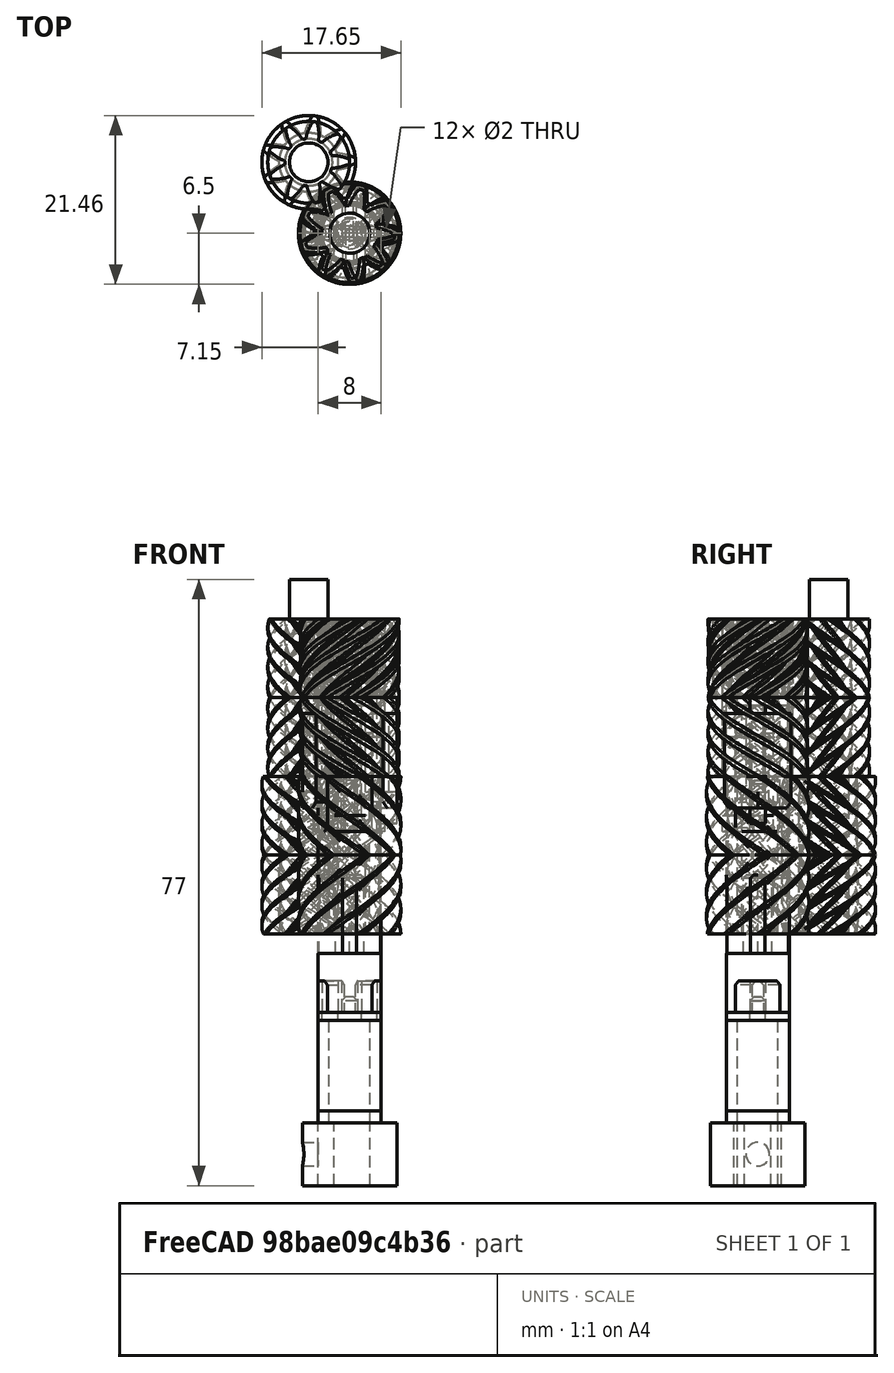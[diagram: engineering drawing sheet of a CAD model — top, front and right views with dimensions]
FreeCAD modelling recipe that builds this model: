
FCSTD DOCUMENT  (FreeCAD 0.19R24276 (Git))
Label: G-mini_inner-gear_011
License: All rights reserved
LicenseURL: http://en.wikipedia.org/wiki/All_rights_reserved
objects: Part::Cylinder×51, Part::Cut×37, Part::Compound×25, Part::FeaturePython×15, Part::Box×13, Part::Chamfer×11, Mesh::Feature×4
note: 152 computed .brp shape members not serialized (recipe doc carries the construction recipe); baked Part::Feature solids carry a one-line shape summary decoded from their .brp

FEATURE [Part::Cylinder] Cylinder016  label="Válec016"
  Angle = 360
  AttacherType = Attacher::AttachEngine3D
  Height = 60
  Placement = pos=(10.4,0,-20) rot=(0,0,1;0rad)
  Radius = 2.55
FEATURE [Part::Cylinder] Cylinder017  label="Válec017"
  Angle = 360
  AttacherType = Attacher::AttachEngine3D
  Height = 60
  Placement = pos=(10.4,0,40) rot=(0,0,1;0rad)
  Radius = 2.55
FEATURE [Part::Cylinder] Cylinder018  label="Válec018"
  Angle = 360
  AttacherType = Attacher::AttachEngine3D
  Height = 60
  Placement = pos=(10.4,0,-20) rot=(0,0,1;0rad)
  Radius = 2.55
FEATURE [Part::Cylinder] Cylinder019  label="Válec019"
  Angle = 360
  AttacherType = Attacher::AttachEngine3D
  Height = 60
  Placement = pos=(10.4,0,40) rot=(0,0,1;0rad)
  Radius = 2.55
FEATURE [Part::FeaturePython] wormgear025  # WARN: FeaturePython — macro-defined, semantics opaque (R4)
  AttacherType = Attacher::AttachEngine3D
  Placement = pos=(10.4,0,0) rot=(0,0,1;0.977384rad)
  beta = 37.1583
  clearance = 0.25
  diameter = 9.5
  head = 0.5
  height = 10
  module = 0.8
  pressure_angle = 20
  reverse_pitch = true
  teeth = 9
  version = 0.0.3
FEATURE [Part::Cut] Cut005
  Base = -> wormgear025
  Tool = -> Cylinder018
FEATURE [Part::FeaturePython] wormgear031  # WARN: FeaturePython — macro-defined, semantics opaque (R4)
  AttacherType = Attacher::AttachEngine3D
  Placement = pos=(10.4,0,-10) rot=(0,0,1;0.991347rad)
  beta = 37.1583
  clearance = 0.25
  diameter = 9.5
  head = 0.5
  height = 10
  module = 0.8
  pressure_angle = 20
  reverse_pitch = false
  teeth = 9
  version = 0.0.3
FEATURE [Part::Cut] Cut002
  Base = -> wormgear031
  Tool = -> Cylinder016
FEATURE [Part::FeaturePython] wormgear032  # WARN: FeaturePython — macro-defined, semantics opaque (R4)
  AttacherType = Attacher::AttachEngine3D
  Placement = pos=(10.4,0,20) rot=(0,0,1;0.959931rad)
  beta = 41.9872
  clearance = 0.25
  diameter = 8
  head = 0.5
  height = 10
  module = 0.8
  pressure_angle = 20
  reverse_pitch = true
  teeth = 9
  version = 0.0.3
FEATURE [Part::Cut] Cut003
  Base = -> wormgear032
  Tool = -> Cylinder019
FEATURE [Part::FeaturePython] wormgear033  # WARN: FeaturePython — macro-defined, semantics opaque (R4)
  AttacherType = Attacher::AttachEngine3D
  Placement = pos=(10.4,0,10) rot=(0,0,1;0.977384rad)
  beta = 41.9872
  clearance = 0.25
  diameter = 8
  head = 0.5
  height = 10
  module = 0.8
  pressure_angle = 20
  reverse_pitch = false
  teeth = 9
  version = 0.0.3
FEATURE [Part::Cut] Cut004
  Base = -> wormgear033
  Tool = -> Cylinder017
FEATURE [Part::Compound] Compound002  label="gearovina-mini_vnejsi-kolecko_1"
  Links = -> [Cut002,Cut004,Cut003,Cut005]
FEATURE [Part::Cylinder] Cylinder025  label="Válec025"
  Angle = 360
  AttacherType = Attacher::AttachEngine3D
  Height = 5
  Placement = pos=(10.4,0,30) rot=(0,0,1;0rad)
  Radius = 2.45
FEATURE [Part::Compound] Compound007  label="gearovina-mini_vnejsi-kolecko001"
  Links = -> [Compound002,Cylinder025]
  Placement = pos=(0,0,0) rot=(0,0,1;2.0944rad)
FEATURE [Part::Cylinder] Cylinder028  label="Válec028"
  Angle = 360
  AttacherType = Attacher::AttachEngine3D
  Height = 60
  Placement = pos=(0,0,-20) rot=(0,0,1;0rad)
  Radius = 2.55
FEATURE [Part::Cylinder] Cylinder029  label="Válec029"
  Angle = 360
  AttacherType = Attacher::AttachEngine3D
  Height = 60
  Placement = pos=(0,0,-20) rot=(0,0,1;0rad)
  Radius = 2.55
FEATURE [Part::FeaturePython] wormgear036  # WARN: FeaturePython — macro-defined, semantics opaque (R4)
  AttacherType = Attacher::AttachEngine3D
  Placement = pos=(0,0,0) rot=(0,0,1;1.11876rad)
  beta = 41.9872
  clearance = 0.1
  diameter = 10
  head = 0.5
  height = 10
  module = 1
  pressure_angle = 20
  reverse_pitch = true
  teeth = 9
  version = 0.0.3
FEATURE [Part::Cut] Cut009
  Base = -> wormgear036
  Tool = -> Cylinder028
FEATURE [Part::FeaturePython] wormgear037  # WARN: FeaturePython — macro-defined, semantics opaque (R4)
  AttacherType = Attacher::AttachEngine3D
  Placement = pos=(0,0,-10) rot=(0,0,1;0.991347rad)
  beta = 41.9872
  clearance = 0.1
  diameter = 10
  head = 0.5
  height = 10
  module = 1
  pressure_angle = 20
  reverse_pitch = false
  teeth = 9
  version = 0.0.3
FEATURE [Part::Cut] Cut008
  Base = -> wormgear037
  Tool = -> Cylinder029
FEATURE [Part::Compound] Compound1283  label="G-midi_outer-gear"
  Links = -> [Cut009,Cut008]
FEATURE [Part::FeaturePython] Tube001  # WARN: FeaturePython — macro-defined, semantics opaque (R4)
  AttacherType = Attacher::AttachEngine3D
  Height = 10
  InnerRadius = 2
  OuterRadius = 4
  Placement = pos=(0,0,-10) rot=(0,0,1;0rad)
FEATURE [Part::Cylinder] Cylinder  label="Válec"
  Angle = 360
  AttacherType = Attacher::AttachEngine3D
  Height = 10
  Radius = 4
FEATURE [Part::FeaturePython] wormgear035  # WARN: FeaturePython — macro-defined, semantics opaque (R4)
  AttacherType = Attacher::AttachEngine3D
  Placement = pos=(0,0,20) rot=(0,0,1;1.6057rad)
  beta = 33.2066
  clearance = 0.25
  diameter = 11
  head = 0
  height = 10
  module = 0.8
  pressure_angle = 20
  reverse_pitch = false
  teeth = 9
  version = 0.0.3
FEATURE [Part::FeaturePython] wormgear038  # WARN: FeaturePython — macro-defined, semantics opaque (R4)
  AttacherType = Attacher::AttachEngine3D
  Placement = pos=(0,0,10) rot=(0,0,1;1.6057rad)
  beta = 33.2066
  clearance = 0.25
  diameter = 11
  head = 0
  height = 10
  module = 0.8
  pressure_angle = 20
  reverse_pitch = true
  teeth = 9
  version = 0.0.3
FEATURE [Part::Compound] Compound011
  Links = -> [wormgear035,wormgear038,Tube001,Cylinder]
FEATURE [Part::Cylinder] Cylinder2021  label="Válec2021"
  Angle = 360
  AttacherType = Attacher::AttachEngine3D
  Height = 12
  Placement = pos=(0,0,-20) rot=(0,0,1;0rad)
  Radius = 4
FEATURE [Part::Cylinder] Cylinder2022  label="Válec2022"
  Angle = 360
  AttacherType = Attacher::AttachEngine3D
  Height = 6
  Placement = pos=(0,0,-14) rot=(0,0,1;0rad)
  Radius = 2
FEATURE [Part::Cylinder] Cylinder2023  label="Válec2023"
  Angle = 360
  AttacherType = Attacher::AttachEngine3D
  Height = 20
  Placement = pos=(-4,0,-20) rot=(0,0,-1;1.5708rad)
  Radius = 1
FEATURE [Part::Cylinder] Cylinder2024  label="Válec2024"
  Angle = 360
  AttacherType = Attacher::AttachEngine3D
  Height = 12
  Placement = pos=(0,0,-20) rot=(0,0,1;0rad)
  Radius = 1
FEATURE [Part::FeaturePython] wormgear073  # WARN: FeaturePython — macro-defined, semantics opaque (R4)
  AttacherType = Attacher::AttachEngine3D
  Placement = pos=(0,0,20) rot=(0,0,1;0.881391rad)
  beta = 38.6598
  clearance = 0.25
  diameter = 9
  head = 0.5
  height = 10
  module = 0.8
  pressure_angle = 20
  reverse_pitch = false
  teeth = 9
  version = 0.0.3
FEATURE [Part::Cut] Cut481
  Base = -> Cylinder2021
  Tool = -> Cylinder2024
FEATURE [Part::Box] Box421  label="Krychle421"
  AttacherType = Attacher::AttachEngine3D
  Height = 12
  Length = 16
  Placement = pos=(5.65685,-5.65685,-20) rot=(0,0,1;2.35619rad)
  Width = 8
FEATURE [Part::Cut] Cut485
  Base = -> Cut481
  Tool = -> Box421
FEATURE [Part::Cylinder] Cylinder2025  label="Válec2025"
  Angle = 360
  AttacherType = Attacher::AttachEngine3D
  Height = 20
  Placement = pos=(4,0,-20) rot=(0,0,-1;1.5708rad)
  Radius = 1
FEATURE [Part::Compound] Compound650
  Links = -> [Cylinder2025,Cylinder2023]
  Placement = pos=(0,0,24) rot=(0,0,1;0rad)
FEATURE [Part::Cylinder] Cylinder2026  label="Válec2026"
  Angle = 360
  AttacherType = Attacher::AttachEngine3D
  Height = 2
  Placement = pos=(-4,0,-20) rot=(0,0,-1;1.5708rad)
  Radius = 2
FEATURE [Part::Cylinder] Cylinder2027  label="Válec2027"
  Angle = 360
  AttacherType = Attacher::AttachEngine3D
  Height = 2
  Placement = pos=(0,0,18) rot=(0,0,1;0rad)
  Radius = 4
FEATURE [Part::Compound] Compound647
  Links = -> [wormgear073,Cylinder2027]
FEATURE [Part::Cylinder] Cylinder2028  label="Válec2028"
  Angle = 360
  AttacherType = Attacher::AttachEngine3D
  Height = 15
  Placement = pos=(0,0,19) rot=(0,0,1;0rad)
  Radius = 2.6
FEATURE [Part::Cut] Cut480
  Base = -> Compound647
  Tool = -> Cylinder2028
FEATURE [Part::Cut] Cut483
  Base = -> Cut480
  Tool = -> Compound650
FEATURE [Part::Cylinder] Cylinder2029  label="Válec2029"
  Angle = 360
  AttacherType = Attacher::AttachEngine3D
  Height = 20
  Placement = pos=(4,0,-20) rot=(0,0,-1;1.5708rad)
  Radius = 1
FEATURE [Part::Cylinder] Cylinder2030  label="Válec2030"
  Angle = 360
  AttacherType = Attacher::AttachEngine3D
  Height = 2
  Placement = pos=(4,0,-20) rot=(0,0,-1;1.5708rad)
  Radius = 2
FEATURE [Part::Compound] Compound651
  Links = -> [Cylinder2030,Cylinder2026]
  Placement = pos=(0,0,24) rot=(0,0,1;0rad)
FEATURE [Part::Box] Box422  label="Krychle422"
  AttacherType = Attacher::AttachEngine3D
  Height = 12
  Length = 16
  Placement = pos=(-5.65685,-5.65685,-20) rot=(0,0,1;0.785398rad)
  Width = 8
FEATURE [Part::Cut] Cut487
  Base = -> Cut485
  Tool = -> Box422
FEATURE [Part::Cut] Cut484
  Base = -> Cut487
  Placement = pos=(0,0,0) rot=(0,0,1;3.14159rad)
  Tool = -> Cylinder2029
FEATURE [Part::Cut] Cut486
  Base = -> Cut487
  Tool = -> Cylinder2029
FEATURE [Part::Compound] Compound649  label="G-midi_sun-sym-mixo004"
  Links = -> [Cut486,Cut484,Cylinder2022]
  Placement = pos=(0,0,26) rot=(0,0,1;0rad)
FEATURE [Part::Chamfer] Chamfer018
  Base = -> Compound649
  Edges = 4 edges r=0.75: [Edge8,Edge11,Edge29,Edge32]
FEATURE [Part::Cut] Cut482
  Base = -> Chamfer018
  Tool = -> Compound651
FEATURE [Part::Chamfer] Chamfer019
  Base = -> Cut482
  Edges = 1 edges r=0.5: [Edge75]
FEATURE [Part::Compound] Compound648  label="G-midi_inner-gear-part-A-lax"
  Links = -> [Cut483,Chamfer019]
FEATURE [Part::Cylinder] Cylinder2031  label="Válec2031"
  Angle = 360
  AttacherType = Attacher::AttachEngine3D
  Height = 12
  Placement = pos=(0,0,-20) rot=(0,0,1;0rad)
  Radius = 4
FEATURE [Part::Cylinder] Cylinder2032  label="Válec2032"
  Angle = 360
  AttacherType = Attacher::AttachEngine3D
  Height = 6
  Placement = pos=(0,0,-14) rot=(0,0,1;0rad)
  Radius = 1
FEATURE [Part::Cylinder] Cylinder2033  label="Válec2033"
  Angle = 360
  AttacherType = Attacher::AttachEngine3D
  Height = 12
  Placement = pos=(0,0,-20) rot=(0,0,1;0rad)
  Radius = 1
FEATURE [Part::Cut] Cut491
  Base = -> Cylinder2031
  Tool = -> Cylinder2033
FEATURE [Part::Box] Box423  label="Krychle423"
  AttacherType = Attacher::AttachEngine3D
  Height = 12
  Length = 16
  Placement = pos=(5.65685,-5.65685,-20) rot=(0,0,1;2.35619rad)
  Width = 8
FEATURE [Part::Cut] Cut488
  Base = -> Cut491
  Tool = -> Box423
FEATURE [Part::Cylinder] Cylinder2034  label="Válec2034"
  Angle = 360
  AttacherType = Attacher::AttachEngine3D
  Height = 20
  Placement = pos=(2.5,0,-20) rot=(0,0,-1;1.5708rad)
  Radius = 1
FEATURE [Part::Box] Box424  label="Krychle424"
  AttacherType = Attacher::AttachEngine3D
  Height = 12
  Length = 16
  Placement = pos=(-5.65685,-5.65685,-20) rot=(0,0,1;0.785398rad)
  Width = 8
FEATURE [Part::Cut] Cut490
  Base = -> Cut488
  Tool = -> Box424
FEATURE [Part::Cut] Cut489
  Base = -> Cut490
  Placement = pos=(0,0,0) rot=(0,0,1;3.14159rad)
  Tool = -> Cylinder2034
FEATURE [Part::Cut] Cut492
  Base = -> Cut490
  Tool = -> Cylinder2034
FEATURE [Part::Compound] Compound1284  label="G-midi_sun-sym-mixo005"
  Links = -> [Cut492,Cut489,Cylinder2032]
  Placement = pos=(0,0,23) rot=(0,0,1;0rad)
FEATURE [Part::Cylinder] Cylinder2035  label="Válec2035"
  Angle = 360
  AttacherType = Attacher::AttachEngine3D
  Height = 20
  Placement = pos=(-2.5,0,-20) rot=(0,0,-1;1.5708rad)
  Radius = 1
FEATURE [Part::Cylinder] Cylinder2036  label="Válec2036"
  Angle = 360
  AttacherType = Attacher::AttachEngine3D
  Height = 20
  Placement = pos=(2.5,0,-20) rot=(0,0,-1;1.5708rad)
  Radius = 1
FEATURE [Part::Cylinder] Cylinder2037  label="Válec2037"
  Angle = 360
  AttacherType = Attacher::AttachEngine3D
  Height = 5
  Placement = pos=(0,0,15) rot=(0,0,1;0rad)
  Radius = 4
FEATURE [Part::Cylinder] Cylinder2038  label="Válec2038"
  Angle = 360
  AttacherType = Attacher::AttachEngine3D
  Height = 15
  Placement = pos=(0,0,19) rot=(0,0,1;0rad)
  Radius = 2.6
FEATURE [Part::FeaturePython] wormgear074  # WARN: FeaturePython — macro-defined, semantics opaque (R4)
  AttacherType = Attacher::AttachEngine3D
  Placement = pos=(0,0,20) rot=(0,0,1;0.881391rad)
  beta = 43.4518
  clearance = 0.1
  diameter = 9.5
  head = 0.5
  height = 10
  module = 1
  pressure_angle = 20
  reverse_pitch = false
  teeth = 9
  version = 0.0.3
FEATURE [Part::Compound] Compound1285
  Links = -> [wormgear074,Cylinder2037]
FEATURE [Part::Cut] Cut493
  Base = -> Compound1285
  Tool = -> Cylinder2038
FEATURE [Part::Compound] Compound1286
  Links = -> [Cylinder2036,Cylinder2035]
  Placement = pos=(0,0,19) rot=(0,0,1;0rad)
FEATURE [Part::Cut] Cut494
  Base = -> Cut493
  Tool = -> Compound1286
FEATURE [Part::Cylinder] Cylinder2039  label="Válec2039"
  Angle = 360
  AttacherType = Attacher::AttachEngine3D
  Height = 16
  Placement = pos=(5,0,4) rot=(0,0,-1;1.5708rad)
  Radius = 1
FEATURE [Part::Cylinder] Cylinder2040  label="Válec2040"
  Angle = 360
  AttacherType = Attacher::AttachEngine3D
  Height = 2
  Placement = pos=(-2.5,0,-20) rot=(0,0,-1;1.5708rad)
  Radius = 2
FEATURE [Part::Cylinder] Cylinder2041  label="Válec2041"
  Angle = 360
  AttacherType = Attacher::AttachEngine3D
  Height = 2
  Placement = pos=(2.5,0,-20) rot=(0,0,-1;1.5708rad)
  Radius = 2
FEATURE [Part::Compound] Compound1287
  Links = -> [Cylinder2041,Cylinder2040]
  Placement = pos=(0,0,23) rot=(0,0,1;0rad)
FEATURE [Part::Chamfer] Chamfer
  Base = -> Compound1284
  Edges = 1 edges r=0.5: [Edge45]
FEATURE [Part::Chamfer] Chamfer020
  Base = -> Chamfer
  Edges = 4 edges r=0.5: [Edge13,Edge14,Edge34,Edge35]
FEATURE [Part::Compound] Compound  label="G-mini_inner-gear"
  Links = -> [Chamfer020,Cut494]
FEATURE [Part::Cylinder] Cylinder2042  label="Válec2042"
  Angle = 360
  AttacherType = Attacher::AttachEngine3D
  Height = 2
  Placement = pos=(-2.5,0,-20) rot=(0,0,-1;1.5708rad)
  Radius = 2
FEATURE [Part::Cylinder] Cylinder2043  label="Válec2043"
  Angle = 360
  AttacherType = Attacher::AttachEngine3D
  Height = 2
  Placement = pos=(2.5,0,-20) rot=(0,0,-1;1.5708rad)
  Radius = 2
FEATURE [Part::Compound] Compound1288
  Links = -> [Cylinder2043,Cylinder2042]
  Placement = pos=(0,0,23) rot=(0,0,1;1.5708rad)
FEATURE [Part::Cylinder] Cylinder2044  label="Válec2044"
  Angle = 360
  AttacherType = Attacher::AttachEngine3D
  Height = 2
  Placement = pos=(-2.5,0,-20) rot=(0,0,-1;1.5708rad)
  Radius = 2
FEATURE [Part::Cylinder] Cylinder2045  label="Válec2045"
  Angle = 360
  AttacherType = Attacher::AttachEngine3D
  Height = 2
  Placement = pos=(2.5,0,-20) rot=(0,0,-1;1.5708rad)
  Radius = 2
FEATURE [Part::Compound] Compound1289
  Links = -> [Cylinder2045,Cylinder2044]
  Placement = pos=(0,0,23) rot=(0,0,1;0rad)
FEATURE [Part::FeaturePython] wormgear075  # WARN: FeaturePython — macro-defined, semantics opaque (R4)
  AttacherType = Attacher::AttachEngine3D
  Placement = pos=(0,0,20) rot=(0,0,1;0.881391rad)
  beta = 43.4518
  clearance = 0.1
  diameter = 9.5
  head = 0.5
  height = 10
  module = 1
  pressure_angle = 20
  reverse_pitch = false
  teeth = 9
  version = 0.0.3
FEATURE [Part::Cylinder] Cylinder2046  label="Válec2046"
  Angle = 360
  AttacherType = Attacher::AttachEngine3D
  Height = 20
  Placement = pos=(-2.5,0,-20) rot=(0,0,-1;1.5708rad)
  Radius = 1
FEATURE [Part::Cylinder] Cylinder2047  label="Válec2047"
  Angle = 360
  AttacherType = Attacher::AttachEngine3D
  Height = 20
  Placement = pos=(2.5,0,-20) rot=(0,0,-1;1.5708rad)
  Radius = 1
FEATURE [Part::Compound] Compound1290
  Links = -> [Cylinder2047,Cylinder2046]
  Placement = pos=(0,0,22) rot=(0,0,1;0rad)
FEATURE [Part::Cylinder] Cylinder2048  label="Válec2048"
  Angle = 360
  AttacherType = Attacher::AttachEngine3D
  Height = 1
  Placement = pos=(0,0,19) rot=(0,0,1;0rad)
  Radius = 4
FEATURE [Part::Compound] Compound1291
  Links = -> [wormgear075,Cylinder2048]
FEATURE [Part::Cylinder] Cylinder2049  label="Válec2049"
  Angle = 360
  AttacherType = Attacher::AttachEngine3D
  Height = 15
  Placement = pos=(0,0,22) rot=(0,0,1;0rad)
  Radius = 2.6
FEATURE [Part::Cut] Cut495
  Base = -> Compound1291
  Tool = -> Cylinder2049
FEATURE [Part::Cut] Cut496
  Base = -> Cut495
  Tool = -> Compound1290
FEATURE [Part::Box] Box425  label="Krychle425"
  AttacherType = Attacher::AttachEngine3D
  Height = 12
  Length = 16
  Placement = pos=(5.65685,-5.65685,-20) rot=(0,0,1;2.35619rad)
  Width = 8
FEATURE [Part::Cylinder] Cylinder2050  label="Válec2050"
  Angle = 360
  AttacherType = Attacher::AttachEngine3D
  Height = 12
  Placement = pos=(0,0,-20) rot=(0,0,1;0rad)
  Radius = 1
FEATURE [Part::Cylinder] Cylinder2051  label="Válec2051"
  Angle = 360
  AttacherType = Attacher::AttachEngine3D
  Height = 4
  Placement = pos=(0,0,-20) rot=(0,0,1;0rad)
  Radius = 4
FEATURE [Part::Cut] Cut501
  Base = -> Cylinder2051
  Tool = -> Cylinder2050
FEATURE [Part::Cut] Cut497
  Base = -> Cut501
  Tool = -> Box425
FEATURE [Part::Cylinder] Cylinder2052  label="Válec2052"
  Angle = 360
  AttacherType = Attacher::AttachEngine3D
  Height = 2
  Placement = pos=(0,0,-18) rot=(0,0,1;0rad)
  Radius = 1
FEATURE [Part::Cylinder] Cylinder2053  label="Válec2053"
  Angle = 360
  AttacherType = Attacher::AttachEngine3D
  Height = 20
  Placement = pos=(2.5,0,-20) rot=(0,0,-1;1.5708rad)
  Radius = 1
FEATURE [Part::Box] Box426  label="Krychle426"
  AttacherType = Attacher::AttachEngine3D
  Height = 12
  Length = 16
  Placement = pos=(-5.65685,-5.65685,-20) rot=(0,0,1;0.785398rad)
  Width = 8
FEATURE [Part::Cut] Cut499
  Base = -> Cut497
  Tool = -> Box426
FEATURE [Part::Cut] Cut498
  Base = -> Cut499
  Placement = pos=(0,0,0) rot=(0,0,1;3.14159rad)
  Tool = -> Cylinder2053
FEATURE [Part::Cut] Cut500
  Base = -> Cut499
  Tool = -> Cylinder2053
FEATURE [Part::Compound] Compound1292  label="G-midi_sun-sym-mixo006"
  Links = -> [Cut500,Cut498,Cylinder2052]
  Placement = pos=(0,0,23) rot=(0,0,1;0rad)
FEATURE [Part::Chamfer] Chamfer021
  Base = -> Compound1292
  Edges = 1 edges r=0.5: [Edge45]
FEATURE [Part::Chamfer] Chamfer022
  Base = -> Chamfer021
  Edges = 4 edges r=0.5: [Edge13,Edge14,Edge34,Edge35]
  Placement = pos=(0,0,12) rot=(0,0,1;0rad)
FEATURE [Part::Compound] Compound1293  label="G-mini_inner-gear-part-A-short"
  Links = -> [Cut496,Chamfer022]
FEATURE [Part::Box] Box023  label="Krychle023"
  AttacherType = Attacher::AttachEngine3D
  Height = 10
  Length = 10
  Placement = pos=(0,-0.9,-20) rot=(0,0,1;0rad)
  Width = 1.8
FEATURE [Part::Box] Box026  label="Krychle026"
  AttacherType = Attacher::AttachEngine3D
  Height = 10
  Length = 10
  Placement = pos=(-0.9,0,-20) rot=(0,0,-1;1.5708rad)
  Width = 1.8
FEATURE [Part::Cylinder] Cylinder048  label="Válec048"
  Angle = 360
  AttacherType = Attacher::AttachEngine3D
  Height = 100
  Placement = pos=(-100,0,-38) rot=(0.57735,0.57735,0.57735;2.0944rad)
  Radius = 1.5
FEATURE [Part::Compound] Compound024
  Links = -> [Cylinder048]
FEATURE [Part::Cylinder] Cylinder049  label="Válec049"
  Angle = 360
  AttacherType = Attacher::AttachEngine3D
  Height = 20
  Placement = pos=(0,0,-32.5) rot=(0,0,1;0rad)
  Radius = 4
FEATURE [Part::Box] Box022  label="Krychle022"
  AttacherType = Attacher::AttachEngine3D
  Height = 8
  Length = 6
  Placement = pos=(-2,-3,-42) rot=(0,0,1;1.5708rad)
  Width = 2
FEATURE [Part::Box] Box025  label="Krychle025"
  AttacherType = Attacher::AttachEngine3D
  Height = 10
  Length = 10
  Placement = pos=(0,0.9,-20) rot=(0,0,1;3.14159rad)
  Width = 1.8
FEATURE [Part::Box] Box024  label="Krychle024"
  AttacherType = Attacher::AttachEngine3D
  Height = 10
  Length = 10
  Placement = pos=(0.9,0,-20) rot=(0,0,1;1.5708rad)
  Width = 1.8
FEATURE [Part::Compound] Compound025
  Links = -> [Box023,Box024,Box025,Box026]
FEATURE [Part::FeaturePython] Tube006  # WARN: FeaturePython — macro-defined, semantics opaque (R4)
  AttacherType = Attacher::AttachEngine3D
  Height = 8
  InnerRadius = 2.6
  OuterRadius = 6
  Placement = pos=(0,0,-42) rot=(0,0,1;0rad)
FEATURE [Part::Cut] Cut025
  Base = -> Tube006
  Tool = -> Compound024
FEATURE [Part::Cut] Cut026
  Base = -> Cut025
  Tool = -> Box022
FEATURE [Part::FeaturePython] Tube007  # WARN: FeaturePython — macro-defined, semantics opaque (R4)
  AttacherType = Attacher::AttachEngine3D
  Height = 20
  InnerRadius = 4
  OuterRadius = 12
  Placement = pos=(0,0,-20) rot=(0,0,1;0rad)
FEATURE [Part::Cut] Cut027
  Base = -> Compound025
  Tool = -> Tube007
FEATURE [Part::Chamfer] Chamfer005
  Base = -> Cut027
  Edges = 6 edges r=0.4: [Edge22,Edge23,Edge34,Edge35,Edge46,Edge47]
FEATURE [Part::Chamfer] Chamfer004
  Base = -> Chamfer005
  Edges = 2 edges r=0.4: [Edge61,Edge62]
  Placement = pos=(0,0,7.5) rot=(0,0,1;0rad)
FEATURE [Part::Cylinder] Cylinder050  label="Válec050"
  Angle = 360
  AttacherType = Attacher::AttachEngine3D
  Height = 10
  Placement = pos=(0,0,-20) rot=(0,0,1;0rad)
  Radius = 1.8
FEATURE [Part::Chamfer] Chamfer006
  Base = -> Cylinder050
  Edges = 1 edges r=0.4: [Edge1]
  Placement = pos=(0,0,7.5) rot=(0,0,1;0rad)
FEATURE [Mesh::Feature] Mesh  label="G-mini_inner-gear-short (Meshed)"
FEATURE [Part::FeaturePython] Tube008  # WARN: FeaturePython — macro-defined, semantics opaque (R4)
  AttacherType = Attacher::AttachEngine3D
  Height = 13
  InnerRadius = 2.6
  OuterRadius = 4
  Placement = pos=(0,0,-34) rot=(0,0,1;0rad)
FEATURE [Part::Cylinder] Cylinder2054  label="Válec2054"
  Angle = 360
  AttacherType = Attacher::AttachEngine3D
  Height = 20
  Placement = pos=(-2.5,0,-20) rot=(0,0,-1;1.5708rad)
  Radius = 1
FEATURE [Part::Cylinder] Cylinder2055  label="Válec2055"
  Angle = 360
  AttacherType = Attacher::AttachEngine3D
  Height = 20
  Placement = pos=(2.5,0,-20) rot=(0,0,-1;1.5708rad)
  Radius = 1
FEATURE [Part::Compound] Compound1294
  Links = -> [Cylinder2055,Cylinder2054]
  Placement = pos=(0,0,-1) rot=(0,0,1;0rad)
FEATURE [Part::Box] Box427  label="Krychle427"
  AttacherType = Attacher::AttachEngine3D
  Height = 12
  Length = 16
  Placement = pos=(-5.65685,-5.65685,-20) rot=(0,0,1;0.785398rad)
  Width = 8
FEATURE [Part::Cylinder] Cylinder2056  label="Válec2056"
  Angle = 360
  AttacherType = Attacher::AttachEngine3D
  Height = 2
  Placement = pos=(0,0,-18) rot=(0,0,1;0rad)
  Radius = 1
FEATURE [Part::Cylinder] Cylinder2057  label="Válec2057"
  Angle = 360
  AttacherType = Attacher::AttachEngine3D
  Height = 12
  Placement = pos=(0,0,-20) rot=(0,0,1;0rad)
  Radius = 1
FEATURE [Part::Cylinder] Cylinder2058  label="Válec2058"
  Angle = 360
  AttacherType = Attacher::AttachEngine3D
  Height = 4
  Placement = pos=(0,0,-20) rot=(0,0,1;0rad)
  Radius = 4
FEATURE [Part::Cut] Cut504
  Base = -> Cylinder2058
  Tool = -> Cylinder2057
FEATURE [Part::Box] Box428  label="Krychle428"
  AttacherType = Attacher::AttachEngine3D
  Height = 12
  Length = 16
  Placement = pos=(5.65685,-5.65685,-20) rot=(0,0,1;2.35619rad)
  Width = 8
FEATURE [Part::Cut] Cut505
  Base = -> Cut504
  Tool = -> Box428
FEATURE [Part::Cut] Cut503
  Base = -> Cut505
  Tool = -> Box427
FEATURE [Part::Cylinder] Cylinder2059  label="Válec2059"
  Angle = 360
  AttacherType = Attacher::AttachEngine3D
  Height = 20
  Placement = pos=(2.5,0,-20) rot=(0,0,-1;1.5708rad)
  Radius = 1
FEATURE [Part::Cut] Cut502
  Base = -> Cut503
  Tool = -> Cylinder2059
FEATURE [Part::Cut] Cut506
  Base = -> Cut503
  Placement = pos=(0,0,0) rot=(0,0,1;3.14159rad)
  Tool = -> Cylinder2059
FEATURE [Part::Compound] Compound1295  label="G-midi_sun-sym-mixo007"
  Links = -> [Cut502,Cut506,Cylinder2056]
  Placement = pos=(0,0,23) rot=(0,0,1;0rad)
FEATURE [Part::Chamfer] Chamfer024
  Base = -> Compound1295
  Edges = 1 edges r=0.5: [Edge45]
FEATURE [Part::Chamfer] Chamfer023
  Base = -> Chamfer024
  Edges = 4 edges r=0.5: [Edge13,Edge14,Edge34,Edge35]
  Placement = pos=(0,0,-13) rot=(1,0,0;3.14159rad)
FEATURE [Part::Cylinder] Cylinder2060  label="Válec2060"
  Angle = 360
  AttacherType = Attacher::AttachEngine3D
  Height = 1
  Placement = pos=(0,0,-21) rot=(0,0,1;0rad)
  Radius = 4
FEATURE [Part::Cut] Cut
  Base = -> Cylinder2060
  Tool = -> Compound1294
FEATURE [Part::Compound] Compound1296  label="G-mini_inner-gear-part-B"
  Links = -> [Tube008,Chamfer023,Cut,Cut026]
FEATURE [Mesh::Feature] Mesh001  label="G-mini_inner-gear-shaft (Meshed)"
FEATURE [Mesh::Feature] Mesh003  label="G-mini_inner-gear-part-A-short (Meshed)"
FEATURE [Mesh::Feature] Mesh004  label="G-mini_inner-gear-part-B (Meshed)"
